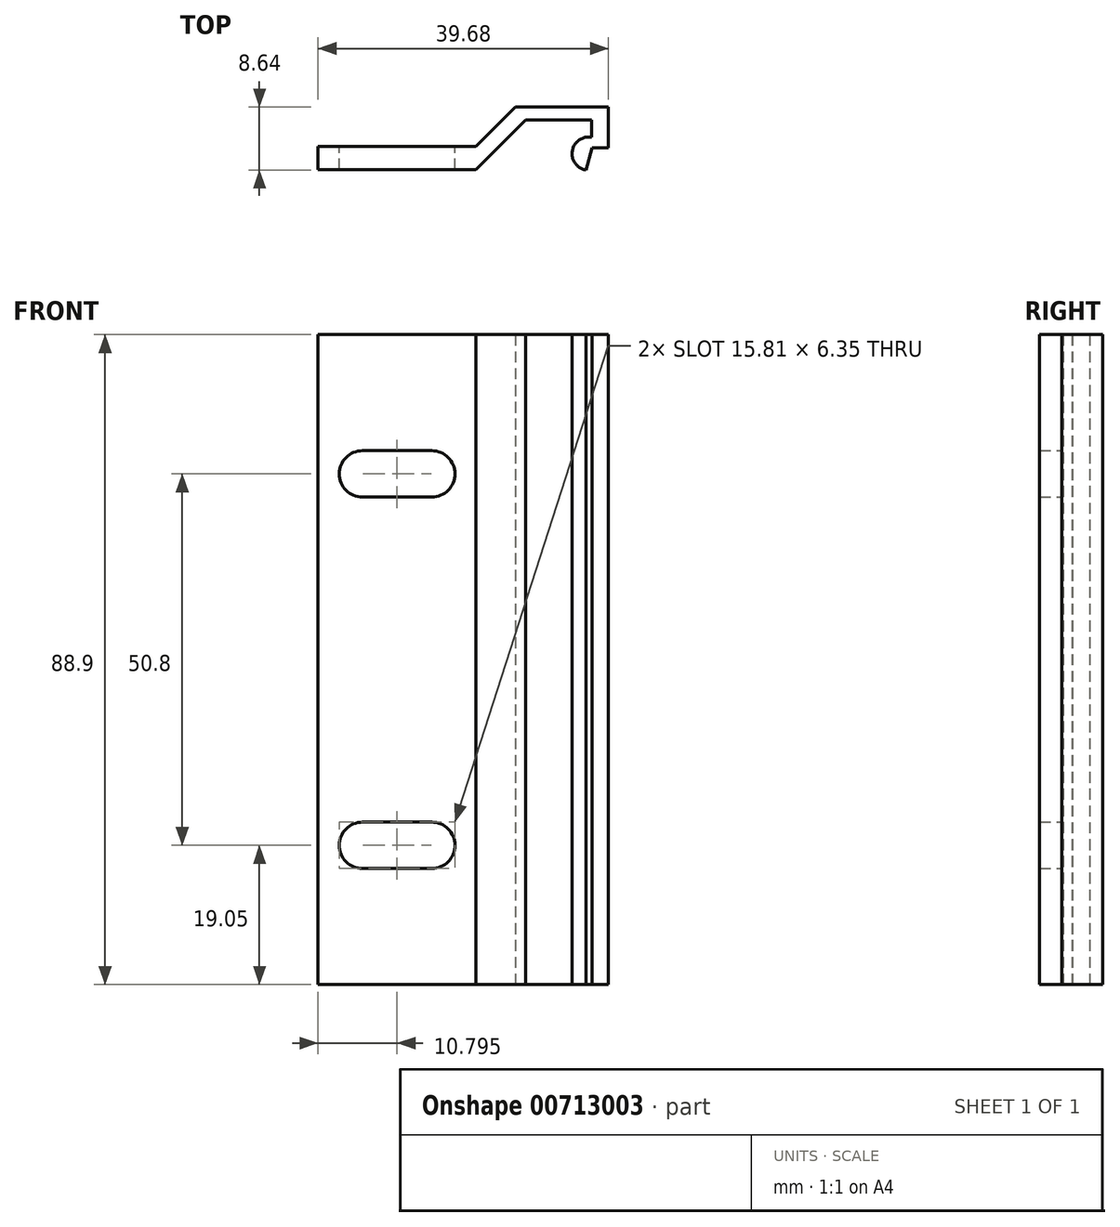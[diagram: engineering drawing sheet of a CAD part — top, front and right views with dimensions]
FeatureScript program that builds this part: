
annotation { "Feature Type Name" : "Feature", "Feature Type Description" : "" }
export const myFeature = defineFeature(function(context is Context, id is Id, definition is map)
    precondition{}
    {
        {
            var Q0;
            Q0=qCreatedBy(makeId("Front.planeOp"),FACE);
            var sketch = newSketch(context, id + "F0", { "sketchPlane" : qUnion([Q0])});
            skLineSegment(sketch, "E0", {"start": v(0, 0) * mm, "end": v(21.6, 0) * mm});
            skLineSegment(sketch, "E1", {"start": v(0, 0) * mm, "end": v(0, -3.18) * mm});
            skLineSegment(sketch, "E2", {"start": v(0, -3.18) * mm, "end": v(21.59, -3.18) * mm});
            skLineSegment(sketch, "E3", {"start": v(21.59, -3.18) * mm, "end": v(28.38, 3.61) * mm});
            skLineSegment(sketch, "E4", {"start": v(21.59, 0) * mm, "end": v(26.98, 5.39) * mm});
            skLineSegment(sketch, "E5", {"start": v(26.98, 5.39) * mm, "end": v(39.68, 5.39) * mm});
            skLineSegment(sketch, "E6", {"start": v(39.68, 5.39) * mm, "end": v(39.68, -0.2) * mm});
            skLineSegment(sketch, "E7", {"start": v(39.68, -0.2) * mm, "end": v(37.41, -0.2) * mm});
            skLineSegment(sketch, "E8", {"start": v(37.41, -0.2) * mm, "end": v(36.6, -3.25) * mm});
            skLineSegment(sketch, "E9", {"start": v(36.6, -3.25) * mm, "end": v(37.4, 1.26) * mm});
            skLineSegment(sketch, "E10", {"start": v(37.4, 1.26) * mm, "end": v(37.4, 3.61) * mm});
            skLineSegment(sketch, "E11", {"start": v(37.4, 3.61) * mm, "end": v(28.38, 3.61) * mm});
            skArc(sketch, "E12", {"start": v(37.4, 1.26) * mm, "mid": v(34.74, -0.6) * mm, "end": v(36.6, -3.25) * mm});
            skSolve(sketch);
        }
        {
            var Q0;
            Q0 = qSketchRegion(id + "F0", true);
            extrude(context, id + "F1", {"entities" : qUnion([Q0]), "depth" : 88.9 * mm, "offsetDistance" : 25.4 * mm});
        }
        {
            var Q0;
            Q0=makeQuery(id+"F1.opExtrude","SWEPT_FACE",FACE,{"disambiguationData":[OSD([sQuery(id+"F0.wireOp",EDGE,"E0")])]});
            var sketch = newSketch(context, id + "F2", { "sketchPlane" : qUnion([Q0])});
            skLineSegment(sketch, "E13.0", {"start": v(21.6, -88.9) * mm, "end": v(21.6, 0) * mm, "construction": true});
            skLineSegment(sketch, "E14.0.1", {"start": v(21.6, 0) * mm, "end": v(21.6, -88.9) * mm, "construction": true});
            skLineSegment(sketch, "E15.0", {"start": v(0, -88.9) * mm, "end": v(0, 0) * mm, "construction": true});
            skLineSegment(sketch, "E16.0", {"start": v(0, 0) * mm, "end": v(21.6, 0) * mm, "construction": true});
            skLineSegment(sketch, "E17.0", {"start": v(0, -88.9) * mm, "end": v(21.6, -88.9) * mm, "construction": true});
            skPoint(sketch, "E18", {"position": v(0, -44.45) * mm});
            skPoint(sketch, "E19", {"position": v(10.8, 0) * mm});
            skLineSegment(sketch, "E20", {"start": v(10.8, 0) * mm, "end": v(10.8, -88.9) * mm});
            skLineSegment(sketch, "E21", {"start": v(0, -44.45) * mm, "end": v(21.6, -44.45) * mm});
            skLineSegment(sketch, "E22.bottom", {"start": v(6.06, -15.88) * mm, "end": v(15.53, -15.88) * mm});
            skLineSegment(sketch, "E22.top", {"start": v(6.06, -22.23) * mm, "end": v(15.53, -22.23) * mm});
            skLineSegment(sketch, "E22.left", {"start": v(6.06, -15.87) * mm, "end": v(6.06, -22.23) * mm, "construction": true});
            skLineSegment(sketch, "E22.right", {"start": v(15.53, -15.87) * mm, "end": v(15.53, -22.23) * mm, "construction": true});
            skArc(sketch, "E23", {"start": v(6.06, -15.87) * mm, "mid": v(2.89, -19.05) * mm, "end": v(6.06, -22.22) * mm});
            skArc(sketch, "E24", {"start": v(15.53, -22.22) * mm, "mid": v(18.7, -19.05) * mm, "end": v(15.53, -15.87) * mm});
            skLineSegment(sketch, "E25", {"start": v(2.89, -19.05) * mm, "end": v(18.7, -19.05) * mm, "construction": true});
            skLineSegment(sketch, "E26.bottom", {"start": v(6.06, -66.67) * mm, "end": v(15.53, -66.67) * mm});
            skLineSegment(sketch, "E26.top", {"start": v(6.06, -73.02) * mm, "end": v(15.53, -73.02) * mm});
            skLineSegment(sketch, "E26.left", {"start": v(6.06, -66.68) * mm, "end": v(6.06, -73.02) * mm, "construction": true});
            skLineSegment(sketch, "E26.right", {"start": v(15.53, -66.68) * mm, "end": v(15.53, -73.02) * mm, "construction": true});
            skArc(sketch, "E27", {"start": v(6.06, -66.68) * mm, "mid": v(2.89, -69.85) * mm, "end": v(6.06, -73.03) * mm});
            skArc(sketch, "E28", {"start": v(15.53, -73.03) * mm, "mid": v(18.7, -69.85) * mm, "end": v(15.53, -66.68) * mm});
            skLineSegment(sketch, "E29", {"start": v(2.89, -69.85) * mm, "end": v(18.7, -69.85) * mm, "construction": true});
            skPoint(sketch, "E30", {"position": v(10.8, -19.05) * mm});
            skPoint(sketch, "E31", {"position": v(10.8, -69.85) * mm});
            skSolve(sketch);
        }
        {
            var Q0;
            {var subQ5=sQuery(id+"F2.wireOp",EDGE,"E23");Q0=makeQuery(id+"F2.imprint","IMPRINT",FACE,{"disambiguationData":[TD([[makeQuery(id+"F2.imprint","IMPRINT",EDGE,{"derivedFrom":subQ5}),1.0]])]});}
            var Q1;
            {var subQ5=sQuery(id+"F2.wireOp",EDGE,"E24");Q1=makeQuery(id+"F2.imprint","IMPRINT",FACE,{"disambiguationData":[TD([[makeQuery(id+"F2.imprint","IMPRINT",EDGE,{"derivedFrom":subQ5}),1.0]])]});}
            var Q2;
            {var subQ5=sQuery(id+"F2.wireOp",EDGE,"E27");Q2=makeQuery(id+"F2.imprint","IMPRINT",FACE,{"disambiguationData":[TD([[makeQuery(id+"F2.imprint","IMPRINT",EDGE,{"derivedFrom":subQ5}),1.0]])]});}
            var Q3;
            {var subQ5=sQuery(id+"F2.wireOp",EDGE,"E28");Q3=makeQuery(id+"F2.imprint","IMPRINT",FACE,{"disambiguationData":[TD([[makeQuery(id+"F2.imprint","IMPRINT",EDGE,{"derivedFrom":subQ5}),1.0]])]});}
            extrude(context, id + "F3", {"entities" : qUnion([Q0, Q1, Q2, Q3]), "operationType" : NewBodyOperationType.REMOVE, "oppositeDirection" : true, "depth" : 25.4 * mm, "offsetDistance" : 25.4 * mm});
        }
        {
            var Q0;
            Q0=makeQuery(id+"F1.opExtrude","SWEPT_BODY",BODY,{"disambiguationData":[OSD([sQuery(id+"F0.wireOp",EDGE,"E0"),sQuery(id+"F0.wireOp",EDGE,"E1"),sQuery(id+"F0.wireOp",EDGE,"E2"),sQuery(id+"F0.wireOp",EDGE,"E3"),sQuery(id+"F0.wireOp",EDGE,"E4"),sQuery(id+"F0.wireOp",EDGE,"E5"),sQuery(id+"F0.wireOp",EDGE,"E6"),sQuery(id+"F0.wireOp",EDGE,"E7"),sQuery(id+"F0.wireOp",EDGE,"E8"),sQuery(id+"F0.wireOp",EDGE,"E10"),sQuery(id+"F0.wireOp",EDGE,"E11"),sQuery(id+"F0.wireOp",EDGE,"E12")])]});
            var Q1;
            Q1=makeQuery(id+"F1.opExtrude","CAP_EDGE",EDGE,{"disambiguationData":[OSD([sQuery(id+"F0.wireOp",EDGE,"E0")])],"isStart":true});
            transform(context, id + "F4", {"entities" : qUnion([Q0]), "transformType" : TransformType.ROTATION, "transformAxis" : qUnion([Q1]), "angle" : 90 * degree, "oppositeDirection" : true, "makeCopy" : false});
        }
    });
